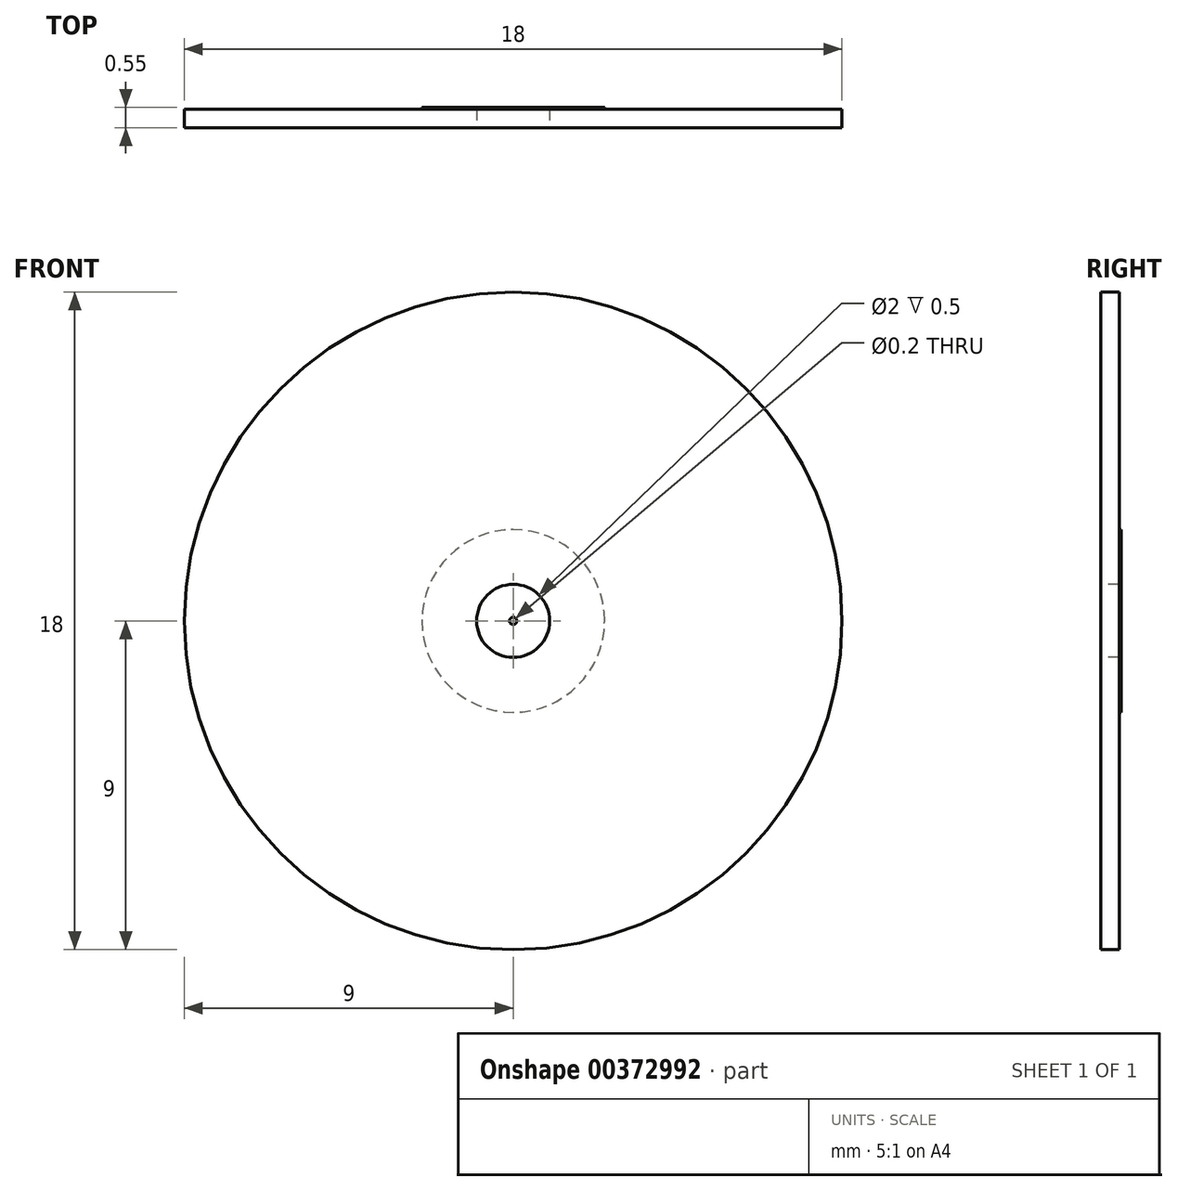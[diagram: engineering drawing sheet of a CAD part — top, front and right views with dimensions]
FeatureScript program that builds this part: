
annotation { "Feature Type Name" : "Feature", "Feature Type Description" : "" }
export const myFeature = defineFeature(function(context is Context, id is Id, definition is map)
    precondition{}
    {
        {
            var Q0;
            Q0=qCreatedBy(makeId("Front.planeOp"),FACE);
            var sketch = newSketch(context, id + "F0", { "sketchPlane" : qUnion([Q0])});
            skCircle(sketch, "E0", {"center": v(0, 0) * mm, "radius": 9 * mm});
            skCircle(sketch, "E1", {"center": v(0, 0) * mm, "radius": 1 * mm});
            skSolve(sketch);
        }
        {
            var Q0;
            Q0 = qSketchRegion(id + "F0", true);
            var Q1;
            Q1 = qConstructionFilter(qBodyType(qCreatedBy(id + "F0" ,EDGE), BodyType.WIRE), ConstructionObject.NO);
            extrude(context, id + "F1", {"entities" : qUnion([Q0]), "surfaceEntities" : qUnion([Q1]), "oppositeDirection" : true, "depth" : 0.5 * mm});
        }
        {
            var Q0;
            Q0=makeQuery(id+"F1.opExtrude","CAP_FACE",FACE,{"disambiguationData":[OSD([sQuery(id+"F0.wireOp",EDGE,"E0"),sQuery(id+"F0.wireOp",EDGE,"E1")])],"isStart":false});
            var sketch = newSketch(context, id + "F2", { "sketchPlane" : qUnion([Q0])});
            skCircle(sketch, "E2", {"center": v(0, 0) * mm, "radius": 2.5 * mm});
            skCircle(sketch, "E3", {"center": v(0, 0) * mm, "radius": 0.1 * mm});
            skSolve(sketch);
        }
        {
            var Q0;
            Q0 = qSketchRegion(id + "F2", true);
            extrude(context, id + "F3", {"entities" : qUnion([Q0]), "operationType" : NewBodyOperationType.ADD, "depth" : 0.05 * mm});
        }
    });
